# Revit family: BWY
name_source: partatom
category: Lighting Fixtures
units: mm (PartAtom-declared; Revit-internal decimal feet)

## family parameters
Cut with Voids When Loaded = No
Host = Face
Light Source = Yes
Maintain Annotation Orientation = No
OmniClass Number = 23.80.70.11.14.11
OmniClass Title = Downlights
Part Type = Normal
Room Calculation Point = No
Round Connector Dimension = Use Diameter
Shared = No

## types (8) — shared parameters
Color Filter = 16777215
Default Elevation = 4' - 0"
Description = Suspended Architectual Linear luminaire
Dimming Lamp Color Temperature Shift = <None>
Housing Finish = Metal - Viscor - White
Lamp = LED
Manufacturer = Visioneering By Viscor
Model = BWY
Tilt Angle = -90.00°
URL = https://viscor.com
Voltage = 120 V
Width = 0' - 2"

## per-type parameters (varying)
| type | Apparent Load | Emit from Line Length | Lamp Wattage | Length | Lens Finish | Photometric Web File |
| BWY2-P48-LED840K04LFUNV | 14 VA | 3' - 8 1/4" | 14 VA | 3' - 8 1/4" | Frosted Acrylic Lens | BWY2-P48-LED840K04LFUNV.ies |
| BWY2-P48-LED840K10LFUNV | 37 VA | 3' - 8 1/4" | 37 VA | 3' - 8 1/4" | Frosted Acrylic Lens | BWY2-P48-LED840K10LFUNV.ies |
| BWY2-P48-LED840K15LFUNV | 59 VA | 3' - 8 1/4" | 59 VA | 3' - 8 1/4" | Frosted Acrylic Lens | BWY2-P48-LED840K15LFUNV.ies |
| BWY2-P24-LED840K15LFUNV | 30 VA | 1' - 10 1/4" | 30 VA | 1' - 10 1/4" | <By Category> | BWY2-P24-LED840K15LFUNV.ies |
| BWY2-P24-LED840K04LFUNV | 7 VA | 1' - 10 1/4" | 7 VA | 1' - 10 1/4" | Frosted Acrylic Lens | BWY2-P24-LED840K04LFUNV.ies |
| BWY2-P24-LED840K10LFUNV | 19 VA | 1' - 10 1/4" | 19 VA | 1' - 10 1/4" | Frosted Acrylic Lens | BWY2-P24-LED840K10LFUNV.ies |
| BWY2-P48-LED840K7.5LFUNV | 28 VA | 3' - 8 1/4" | 28 VA | 3' - 8 1/4" | Frosted Acrylic Lens | BWY2-P48-LED840K7.5LFUNV.ies |
| BWY2-P24-LED840K7.5LFUNV | 14 VA | 1' - 10 1/4" | 14 VA | 1' - 10 1/4" | Frosted Acrylic Lens | BWY2-P24-LED840K7.5LFUNV.ies |

## geometry (parser evidence)
native form markers: Sweep x2
no freeform markers — native parametric forms only
